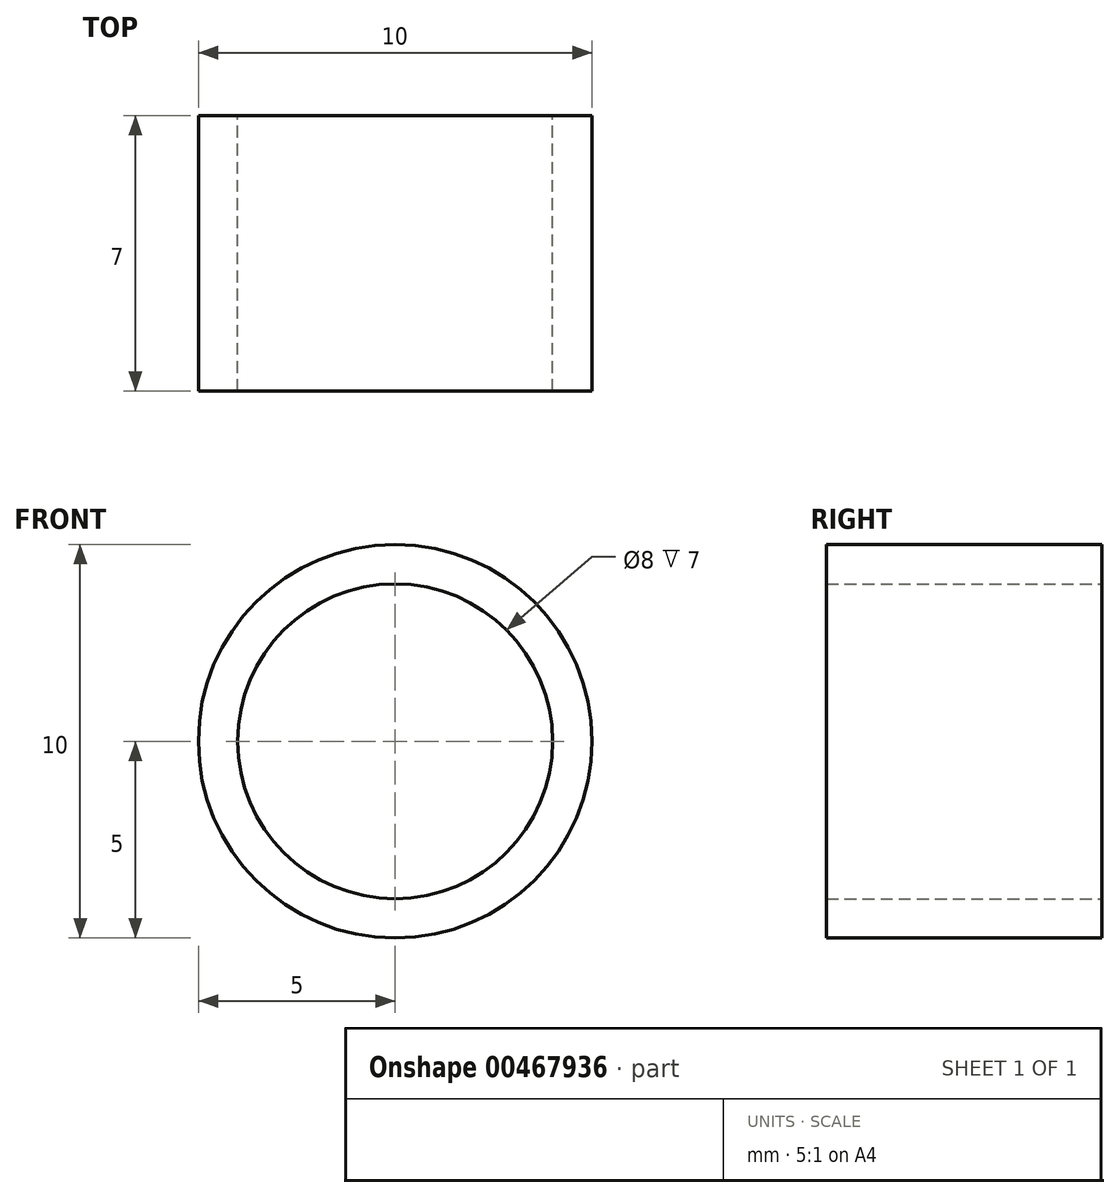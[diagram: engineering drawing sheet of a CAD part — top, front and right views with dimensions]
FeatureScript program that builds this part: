
annotation { "Feature Type Name" : "Feature", "Feature Type Description" : "" }
export const myFeature = defineFeature(function(context is Context, id is Id, definition is map)
    precondition{}
    {
        {
            var Q0;
            Q0=qCreatedBy(makeId("Front.planeOp"),FACE);
            var sketch = newSketch(context, id + "F0", { "sketchPlane" : qUnion([Q0])});
            skCircle(sketch, "E0", {"center": v(0, 0) * mm, "radius": 5 * mm});
            skCircle(sketch, "E1", {"center": v(0, 0) * mm, "radius": 4 * mm});
            skPoint(sketch, "E2", {"position": v(-4, 0) * mm});
            skPoint(sketch, "E3", {"position": v(-5, 0) * mm});
            skPoint(sketch, "E4", {"position": v(4, 0) * mm});
            skLineSegment(sketch, "E5", {"start": v(-4, 0) * mm, "end": v(4, 0) * mm});
            skLineSegment(sketch, "E6", {"start": v(-4, 0) * mm, "end": v(-5, 0) * mm});
            skSolve(sketch);
        }
        {
            var Q0;
            Q0=makeQuery(id+"F0.imprint","IMPRINT",FACE,{"disambiguationData":[TD([[makeQuery(id+"F0.imprint","IMPRINT",EDGE,{"derivedFrom":sQuery(id+"F0.wireOp",EDGE,"E0")}),1.0]])]});
            extrude(context, id + "F1", {"entities" : qUnion([Q0]), "depth" : 7 * mm});
        }
    });
